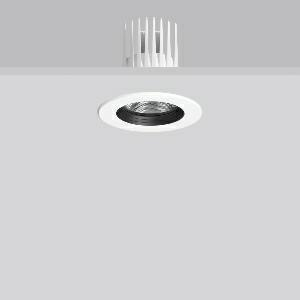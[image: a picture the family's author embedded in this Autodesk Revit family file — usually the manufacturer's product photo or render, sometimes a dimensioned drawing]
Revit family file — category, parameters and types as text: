
# Revit family: heledon_mini_e_901748_002_1_ec84
name_source: partatom
category: Lighting Fixtures
units: mm (PartAtom-declared; Revit-internal decimal feet)

## family parameters
Cut with Voids When Loaded = No
Host = Face
Light Source = No
Part Type = Normal
Room Calculation Point = No
Round Connector Dimension = Use Diameter
Shared = No

## types (1)
- HELEDON mini E (1 x LED Modul 940, 3800 lm, 4000)
    Apparent Load = 29 VA
    Approval mark = CE
    CIE Flux Codes = 100 100 100 100 100
    Color Rendering = 92
    Color Temperature = 4000
    Default Elevation = 1800 mm
    Description = Series: HELEDON mini
Round recessed downlight. Housing: die-cast aluminium, powder-coated. Black plastic ring and recessed LED to prevent glare from the side. Optical assembly with reflector made of MIRO-Silver with 98% total light reflection for outstanding efficiency - can be changed without tools. Best colour rendering index Ra>90. Suitable for Recessed ceiling mounting. Installation without tools thanks to spring fastening system. Including separate LED converter with connecting cable 600 mm.High quality converter without flickering and stroboscopic effect. Through-wiring box (5 pole) available as accessory. The following accessories can be mounted without use of tools: interchangeable lenses, decorative glasses, honeycomb louvre, clear and frosted diffusers, white interchangeable plastic ring. 
Colour: traffic white, matt (RAL 9016)
Diameter: 124 mm
Height: 3 mm
Cut-out diameter: 114 mm
Recess height: 170 mm
Luminaire: recess height: 120 mm
Lamp: LED
Socket: without socket
Colour temperature: 4000K
Colour rendering index (CRI): 92
System power: 29 W
Rated luminous flux: 3800 lm
Luminous efficiency: 131 lm/W
Control gear: Regulated power supply
Protection class: II
Type of protection: IP 20
    Height = 0 mm  [stored 0 ft]
    Lamp = 1 x LED Modul 940
    Lamp Light Flux = 3800 lm
    Lamp count = 1
    Length = 124 mm  [stored 0.406824 ft]
    Lifetime = 50000 h
    Luminous efficacy = 131 lm/W
    Manufacturer = RZB
    ModVariant = No
    Model = 901748.002.1
    Mounting Place = Ceiling
    Mounting Type = Recessed
    Number of Poles = 1
    OnlyDefault = Yes
    Power Factor = 1
    Product Name = HELEDON mini E
    Product group = Recessed downlights
    ProductGroupID = 402
    Protection Class = Protection class II
    Protection Degree = IP 20
    RLX_Detail_Level = 1
    RLX_Emergency_Light_Flux = 0 lm
    RLX_Emergency_Type = 0
    RLX_Emergency_Type_DB = No
    RlxData = <blob elided: 126729 chars, md5=33925e36>
    Socket = socket
    Standby Power = 0 W
    System Light Flux = 3800 lm
    System Power = 29 W
    Type Comments = Product without accessories
    Type Image = 901657.002.jpg
    URL = http://relux.com
    VarID = ---
    Voltage = 230 V
    Voltage Range = 220-240 V
    Weight = 0.00 kg
    Width = 0 mm  [stored 0 ft]

note: [stored X ft] marks values corroborated as IEEE doubles in the binary element streams (Revit-internal decimal feet)

## geometry (parser evidence)
native form markers: Blend x4, Sweep x12
no freeform markers — native parametric forms only
